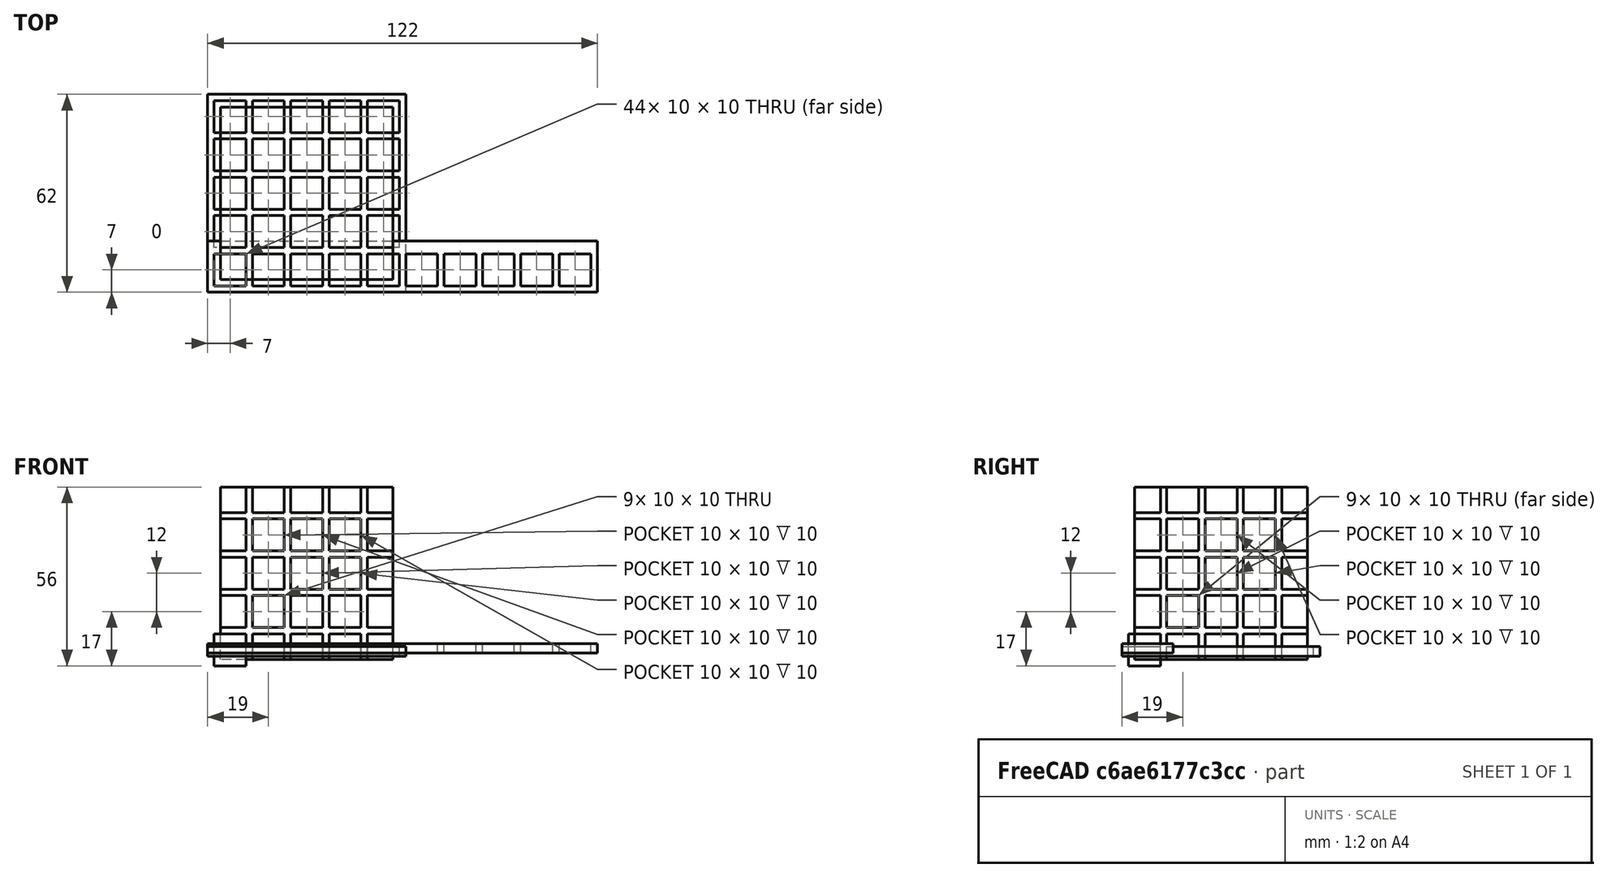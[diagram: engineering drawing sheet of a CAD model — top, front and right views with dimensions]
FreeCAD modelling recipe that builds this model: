
FCSTD DOCUMENT  (FreeCAD 0.21R33694 (Git))
Label: OJT1_T10_R01
License: All rights reserved
LicenseURL: https://en.wikipedia.org/wiki/All_rights_reserved
objects: Part::Box×6, Part::FeaturePython×3, Part::Cut×3
note: 9 computed .brp shape members not serialized (recipe doc carries the construction recipe); baked Part::Feature solids carry a one-line shape summary decoded from their .brp

FEATURE [Part::Box] Box  label="Master_box"
  AttacherType = Attacher::AttachEngine3D
  Height = 10
  Length = 10
  Width = 10
FEATURE [Part::FeaturePython] Array  # Draft array (typed FeaturePython)
  AlwaysSyncPlacement = false
  Angle = 360
  ArrayType = 0
  Axis = (0,0,1)
  Base = -> Box
  Center = (0,0,0)
  Count = 10
  ExpandArray = false
  Fuse = false
  IntervalAxis = (0,0,0)
  IntervalX = (12,0,0)
  IntervalY = (0,100,0)
  IntervalZ = (0,0,100)
  NumberCircles = 3
  NumberPolar = 5
  NumberX = 10
  NumberY = 0
  NumberZ = 0
  PlacementList = 10 placements: arithmetic series from (0,0,0) step (12,0,0) to (108,0,0)
  RadialDistance = 50
  ScaleList = (10) [(1,1,1),(1,1,1),(1,1,1),(1,1,1),(1,1,1),(1,1,1),(1,1,1),(1,1,1),(1,1,1),(1,1,1)]
  Symmetry = 1
  TangentialDistance = 25
FEATURE [Part::Box] Box001  label="Cub"
  AttacherType = Attacher::AttachEngine3D
  Height = 3
  Length = 122
  Placement = pos=(-2,-2,4) rot=(0,0,1;0rad)
  Width = 16
FEATURE [Part::Cut] Cut
  Base = -> Box001
  Tool = -> Array
FEATURE [Part::Box] Box002  label="Master_Box2"
  AttacherType = Attacher::AttachEngine3D
  Height = 10
  Length = 10
  Width = 10
FEATURE [Part::FeaturePython] Array001  # Draft array (typed FeaturePython)
  AlwaysSyncPlacement = false
  Angle = 360
  ArrayType = 0
  Axis = (0,0,1)
  Base = -> Box002
  Center = (0,0,0)
  Count = 25
  ExpandArray = false
  Fuse = false
  IntervalAxis = (0,0,0)
  IntervalX = (12,0,0)
  IntervalY = (0,12,0)
  IntervalZ = (0,0,100)
  NumberCircles = 3
  NumberPolar = 5
  NumberX = 5
  NumberY = 5
  NumberZ = 1
  PlacementList = 25 placements: [(0,0,0),(0,12,0),(0,24,0),(0,36,0),(0,48,0),(12,0,0),(12,12,0),(12,24,0),(12,36,0),(12,48,0),(24,0,0),(24,12,0),(24,24,0),(24,36,0),(24,48,0),(36,0,0),(36,12,0),(36,24,0),(36,36,0),(36,48,0),(48,0,0),(48,12,0),(48,24,0),(48,36,0),(48,48,0)]
  RadialDistance = 50
  ScaleList = (25) [(1,1,1),(1,1,1),(1,1,1),(1,1,1),(1,1,1),(1,1,1),(1,1,1),(1,1,1),(1,1,1),(1,1,1),(1,1,1),(1,1,1),(1,1,1),(1,1,1),(1,1,1),(1,1,1),(1,1,1),(1,1,1),+7 more]
  Symmetry = 1
  TangentialDistance = 25
FEATURE [Part::Box] Box003  label="Cub001"
  AttacherType = Attacher::AttachEngine3D
  Height = 3
  Length = 62
  Placement = pos=(-2,-2,3) rot=(0,0,1;0rad)
  Width = 62
  expr: .Placement.Base.x = -2
  expr: .Placement.Base.y = -2
  expr: .Placement.Base.z = 3
FEATURE [Part::Cut] Cut001
  Base = -> Box003
  Tool = -> Array001
FEATURE [Part::Box] Box004  label="Master_Box3"
  AttacherType = Attacher::AttachEngine3D
  Height = 10
  Length = 10
  Width = 10
FEATURE [Part::FeaturePython] Array002  # Draft array (typed FeaturePython)
  AlwaysSyncPlacement = false
  Angle = 360
  ArrayType = 0
  Axis = (0,0,1)
  Base = -> Box004
  Center = (0,0,0)
  Count = 125
  ExpandArray = false
  Fuse = false
  IntervalAxis = (0,0,0)
  IntervalX = (12,0,0)
  IntervalY = (0,12,0)
  IntervalZ = (0,0,12)
  NumberCircles = 3
  NumberPolar = 5
  NumberX = 5
  NumberY = 5
  NumberZ = 5
  PlacementList = 125 placements: [(0,0,0),(0,0,12),(0,0,24),(0,0,36),(0,0,48),(0,12,0),(0,12,12),(0,12,24),(0,12,36),(0,12,48),(0,24,0),(0,24,12),(0,24,24),(0,24,36),(0,24,48),(0,36,0),(0,36,12),(0,36,24),(0,36,36),(0,36,48),(0,48,0),(0,48,12),(0,48,24),(0,48,36),(0,48,48),(12,0,0),(12,0,12),(12,0,24),(12,0,36),(12,0,48),(12,12,0),(12,12,12),(12,12,24),(12,12,36),(12,12,48),(12,24,0),(12,24,12),(12,24,24),(12,24,36),(12,24,48),+85 more]
  RadialDistance = 50
  ScaleList = (125) [(1,1,1),(1,1,1),(1,1,1),(1,1,1),(1,1,1),(1,1,1),(1,1,1),(1,1,1),(1,1,1),(1,1,1),(1,1,1),(1,1,1),(1,1,1),(1,1,1),(1,1,1),(1,1,1),(1,1,1),(1,1,1),+107 more]
  Symmetry = 1
  TangentialDistance = 25
FEATURE [Part::Box] Box005  label="BAse"
  AttacherType = Attacher::AttachEngine3D
  Height = 54
  Length = 54
  Placement = pos=(2,2,2) rot=(0,0,1;0rad)
  Width = 54
FEATURE [Part::Cut] Cut002
  Base = -> Box005
  Tool = -> Array002
